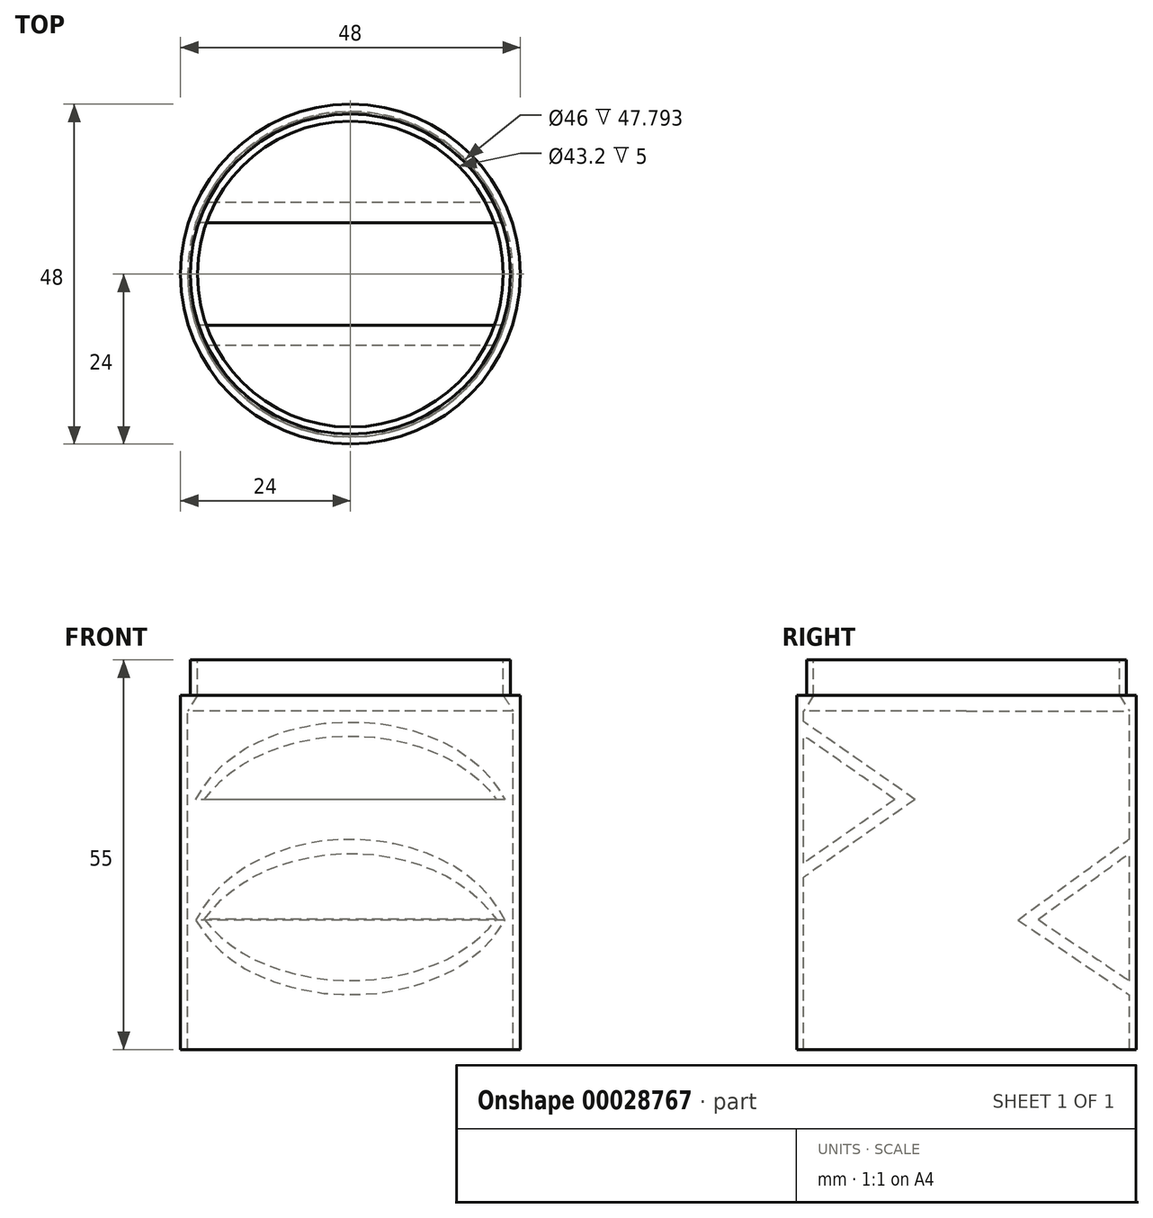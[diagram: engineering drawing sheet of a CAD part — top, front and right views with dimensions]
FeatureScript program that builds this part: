
annotation { "Feature Type Name" : "Feature", "Feature Type Description" : "" }
export const myFeature = defineFeature(function(context is Context, id is Id, definition is map)
    precondition{}
    {
        {
            var Q0;
            Q0=qCreatedBy(makeId("Top.planeOp"),FACE);
            var sketch = newSketch(context, id + "F0", { "sketchPlane" : qUnion([Q0])});
            skCircle(sketch, "E0", {"center": v(0, 0) * mm, "radius": 24 * mm});
            skSolve(sketch);
        }
        {
            var Q0;
            Q0=makeQuery(id+"F0.imprint","IMPRINT",FACE,{"disambiguationData":[TD([[makeQuery(id+"F0.imprint","IMPRINT",EDGE,{"derivedFrom":sQuery(id+"F0.wireOp",EDGE,"E0")}),1.0]])]});
            extrude(context, id + "F1", {"entities" : qUnion([Q0]), "depth" : 50 * mm});
        }
        {
            var Q0;
            Q0=makeQuery(id+"F1.opExtrude","CAP_FACE",FACE,{"disambiguationData":[OSD([sQuery(id+"F0.wireOp",EDGE,"E0")])],"isStart":false});
            var sketch = newSketch(context, id + "F2", { "sketchPlane" : qUnion([Q0])});
            skCircle(sketch, "E1", {"center": v(0, 0) * mm, "radius": 23 * mm});
            skSolve(sketch);
        }
        {
            var Q0;
            Q0=qSketchRegion(id+"F2",true);
            extrude(context, id + "F3", {"entities" : qUnion([Q0]), "operationType" : NewBodyOperationType.REMOVE, "endBound" : BoundingType.THROUGH_ALL, "oppositeDirection" : true, "depth" : 25 * mm});
        }
        {
            var Q0;
            Q0=qCreatedBy(makeId("Front.planeOp"),FACE);
            var sketch = newSketch(context, id + "F4", { "sketchPlane" : qUnion([Q0])});
            skLineSegment(sketch, "E2", {"start": v(0, 0) * mm, "end": v(0, 50) * mm});
            skLineSegment(sketch, "E3.0", {"start": v(-23.5, 50) * mm, "end": v(-23.5, 47) * mm});
            skLineSegment(sketch, "E4", {"start": v(-23.5, 50) * mm, "end": v(-22.6, 50) * mm});
            skLineSegment(sketch, "E5", {"start": v(-22.6, 50) * mm, "end": v(-22.6, 55) * mm});
            skLineSegment(sketch, "E6", {"start": v(-22.6, 55) * mm, "end": v(-21.6, 55) * mm});
            skLineSegment(sketch, "E7", {"start": v(-21.6, 55) * mm, "end": v(-21.6, 50) * mm});
            skLineSegment(sketch, "E8", {"start": v(-21.6, 50) * mm, "end": v(-23.5, 47) * mm});
            skLineSegment(sketch, "E9", {"start": v(-24, 50) * mm, "end": v(-23.5, 50) * mm});
            skSolve(sketch);
        }
        {
            var Q0;
            Q0=qSketchRegion(id+"F4",true);
            var Q1;
            Q1=makeQuery(id+"F3.boolean.opBoolean","COPY",FACE,{"derivedFrom":makeQuery(id+"F3.opExtrude","SWEPT_FACE",FACE,{"disambiguationData":[OSD([sQuery(id+"F2.wireOp",EDGE,"E1")])]})});
            revolve(context, id + "F5", {"operationType" : NewBodyOperationType.ADD, "entities" : qUnion([Q0]), "axis" : qUnion([Q1]), "revolveType" : RevolveType.FULL});
        }
        {
            var Q0;
            Q0=qCreatedBy(makeId("Right.planeOp"),FACE);
            var sketch = newSketch(context, id + "F6", { "sketchPlane" : qUnion([Q0])});
            skCircle(sketch, "E10", {"center": v(0, 27.55) * mm, "radius": 3 * mm});
            skLineSegment(sketch, "E11.rect.bottom", {"start": v(-3, 21.55) * mm, "end": v(3, 21.55) * mm});
            skLineSegment(sketch, "E11.rect.top", {"start": v(-3, 27.55) * mm, "end": v(3, 27.55) * mm});
            skLineSegment(sketch, "E11.rect.left", {"start": v(-3, 21.55) * mm, "end": v(-3, 27.55) * mm});
            skLineSegment(sketch, "E11.rect.right", {"start": v(3, 21.55) * mm, "end": v(3, 27.55) * mm});
            skPoint(sketch, "E11.rect.middle", {"position": v(0, 24.55) * mm});
            skSolve(sketch);
        }
        {
            var Q0;
            Q0=qCreatedBy(makeId("Right.planeOp"),FACE);
            var sketch = newSketch(context, id + "F7", { "sketchPlane" : qUnion([Q0])});
            skLineSegment(sketch, "E12", {"start": v(-23, 46.31) * mm, "end": v(-7.25, 35.31) * mm});
            skLineSegment(sketch, "E13", {"start": v(-7.25, 35.31) * mm, "end": v(-23, 24.31) * mm});
            skLineSegment(sketch, "E14", {"start": v(23, 7.71) * mm, "end": v(7.25, 18.3) * mm});
            skLineSegment(sketch, "E15", {"start": v(7.25, 18.3) * mm, "end": v(23, 29.71) * mm});
            skLineSegment(sketch, "E16", {"start": v(-23, 46.31) * mm, "end": v(-23, 44.31) * mm});
            skLineSegment(sketch, "E17", {"start": v(0, 18.3) * mm, "end": v(0, 35.31) * mm, "construction": true});
            skLineSegment(sketch, "E18", {"start": v(-7.25, 35.31) * mm, "end": v(0, 35.31) * mm, "construction": true});
            skLineSegment(sketch, "E19", {"start": v(0, 18.3) * mm, "end": v(7.25, 18.3) * mm, "construction": true});
            skLineSegment(sketch, "E20", {"start": v(-23, 24.31) * mm, "end": v(0, 24.31) * mm, "construction": true});
            skLineSegment(sketch, "E21", {"start": v(23, 29.71) * mm, "end": v(0, 29.71) * mm, "construction": true});
            skLineSegment(sketch, "E22", {"start": v(0, 29.71) * mm, "end": v(0, 24.31) * mm, "construction": true});
            skLineSegment(sketch, "E23", {"start": v(-23, 46.31) * mm, "end": v(-23, 24.31) * mm, "construction": true});
            skLineSegment(sketch, "E24", {"start": v(23, 29.71) * mm, "end": v(23, 7.71) * mm, "construction": true});
            skLineSegment(sketch, "E25.MirrorCS", {"start": v(-23, 24.31) * mm, "end": v(-23, 26.31) * mm});
            skLineSegment(sketch, "E26", {"start": v(-23, 44.31) * mm, "end": v(-10.11, 35.31) * mm});
            skLineSegment(sketch, "E27", {"start": v(-23, 26.31) * mm, "end": v(-10.11, 35.31) * mm});
            skLineSegment(sketch, "E28", {"start": v(23, 29.71) * mm, "end": v(23, 27.71) * mm});
            skLineSegment(sketch, "E29", {"start": v(23, 7.71) * mm, "end": v(23, 9.71) * mm});
            skLineSegment(sketch, "E30", {"start": v(23, 27.71) * mm, "end": v(10.11, 18.37) * mm});
            skLineSegment(sketch, "E31", {"start": v(23, 9.71) * mm, "end": v(10.11, 18.37) * mm});
            skSolve(sketch);
        }
        {
            var Q0;
            Q0=makeQuery(id+"F7.imprint","IMPRINT",FACE,{"disambiguationData":[TD([[makeQuery(id+"F7.imprint","IMPRINT",EDGE,{"derivedFrom":sQuery(id+"F7.wireOp",EDGE,"E12")}),-1.0]])]});
            var Q1;
            Q1=makeQuery(id+"F7.imprint","IMPRINT",FACE,{"disambiguationData":[TD([[makeQuery(id+"F7.imprint","IMPRINT",EDGE,{"derivedFrom":sQuery(id+"F7.wireOp",EDGE,"E14")}),-1.0]])]});
            extrude(context, id + "F8", {"entities" : qUnion([Q0, Q1]), "operationType" : NewBodyOperationType.ADD, "endBound" : BoundingType.UP_TO_NEXT, "depth" : 25 * mm, "hasSecondDirection" : true, "secondDirectionBound" : SecondDirectionBoundingType.UP_TO_NEXT, "secondDirectionOppositeDirection" : true, "secondDirectionDepth" : 25 * mm});
        }
    });
